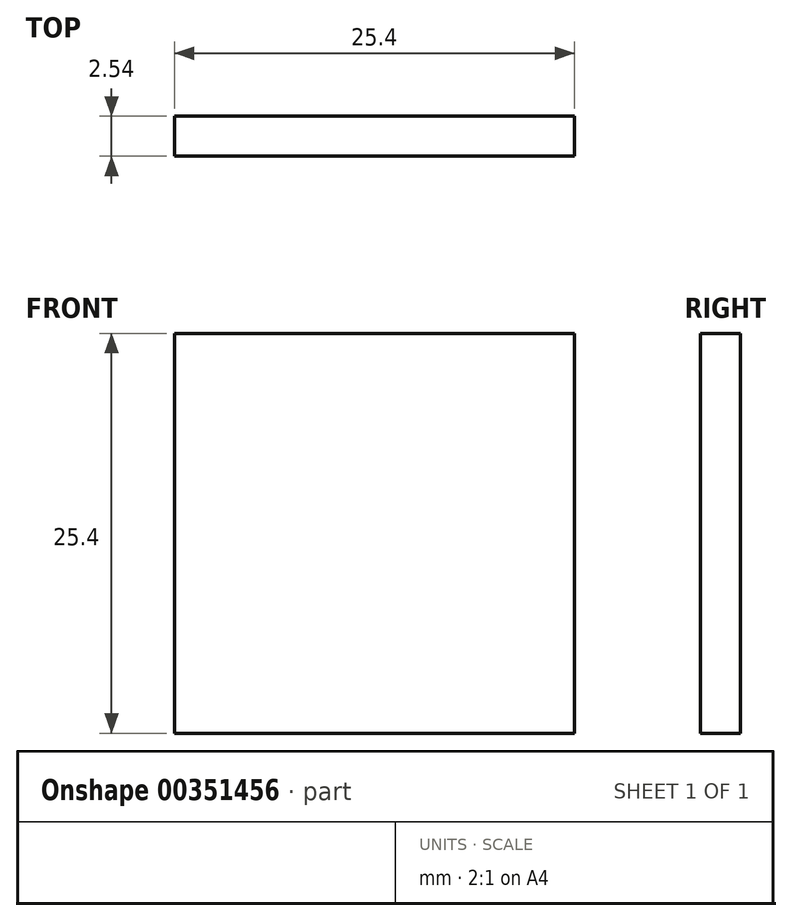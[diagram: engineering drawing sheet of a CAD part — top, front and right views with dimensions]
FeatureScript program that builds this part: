
annotation { "Feature Type Name" : "Feature", "Feature Type Description" : "" }
export const myFeature = defineFeature(function(context is Context, id is Id, definition is map)
    precondition{}
    {
        {
            var Q0;
            Q0=qCreatedBy(makeId("Front.planeOp"),FACE);
            var sketch = newSketch(context, id + "F0", { "sketchPlane" : qUnion([Q0])});
            skLineSegment(sketch, "E0.bottom", {"start": v(19.49, 5.14) * mm, "end": v(44.89, 5.14) * mm});
            skLineSegment(sketch, "E0.top", {"start": v(19.49, -20.26) * mm, "end": v(44.89, -20.26) * mm});
            skLineSegment(sketch, "E0.left", {"start": v(19.49, 5.14) * mm, "end": v(19.49, -20.26) * mm});
            skLineSegment(sketch, "E0.right", {"start": v(44.89, 5.14) * mm, "end": v(44.89, -20.26) * mm});
            skSolve(sketch);
        }
        {
            var Q0;
            Q0=makeQuery(id+"F0.imprint","IMPRINT",FACE,{"disambiguationData":[TD([[makeQuery(id+"F0.imprint","IMPRINT",EDGE,{"derivedFrom":sQuery(id+"F0.wireOp",EDGE,"E0.bottom")}),-1.0]])]});
            extrude(context, id + "F1", {"entities" : qUnion([Q0]), "depth" : 2.54 * mm});
        }
    });
